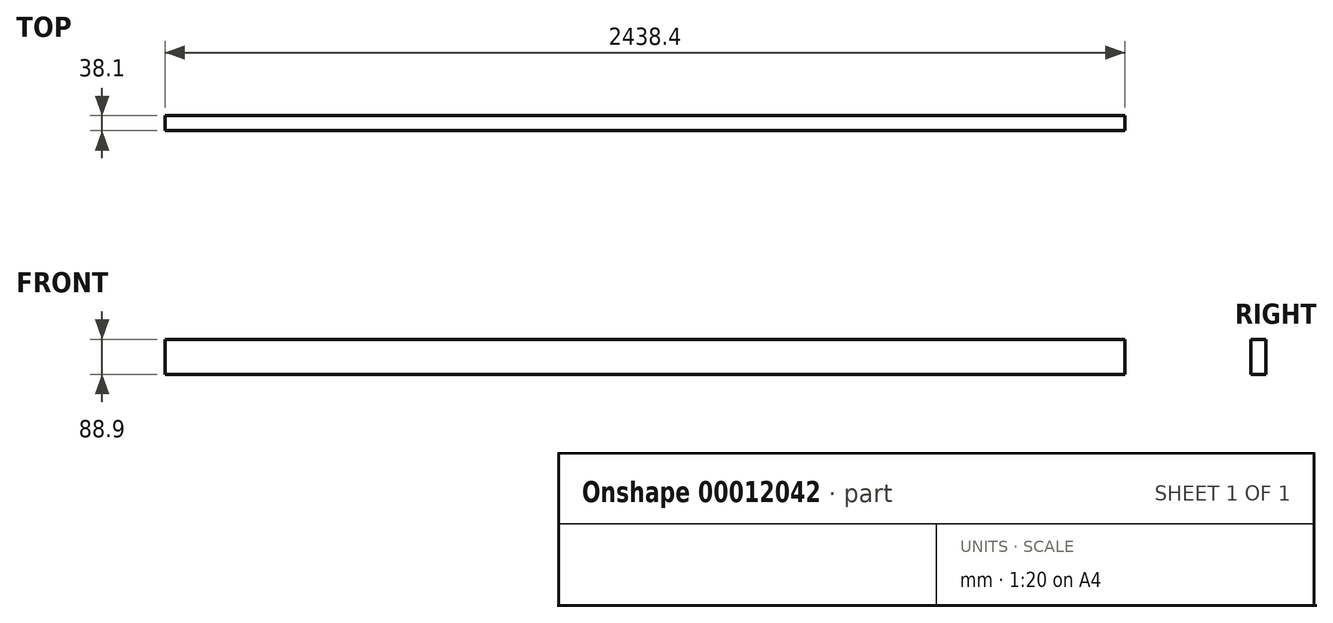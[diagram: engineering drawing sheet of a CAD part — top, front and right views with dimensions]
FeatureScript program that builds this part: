
annotation { "Feature Type Name" : "Feature", "Feature Type Description" : "" }
export const myFeature = defineFeature(function(context is Context, id is Id, definition is map)
    precondition{}
    {
        {
            var Q0;
            Q0=qCreatedBy(makeId("Right.planeOp"),FACE);
            var sketch = newSketch(context, id + "F1", { "sketchPlane" : qUnion([Q0])});
            skLineSegment(sketch, "E0.rect.bottom", {"start": v(19.05, 44.45) * mm, "end": v(-19.05, 44.45) * mm});
            skLineSegment(sketch, "E0.rect.top", {"start": v(19.05, -44.45) * mm, "end": v(-19.05, -44.45) * mm});
            skLineSegment(sketch, "E0.rect.left", {"start": v(19.05, 44.45) * mm, "end": v(19.05, -44.45) * mm});
            skLineSegment(sketch, "E0.rect.right", {"start": v(-19.05, 44.45) * mm, "end": v(-19.05, -44.45) * mm});
            skPoint(sketch, "E0.rect.middle", {"position": v(0, 0) * mm});
            skSolve(sketch);
        }
        {
            var Q0;
            Q0=makeQuery(id+"F1.imprint","IMPRINT",FACE,{"disambiguationData":[TD([[makeQuery(id+"F1.imprint","IMPRINT",EDGE,{"derivedFrom":sQuery(id+"F1.wireOp",EDGE,"E0.rect.bottom")}),1.0]])]});
            extrude(context, id + "F0", {"entities" : qUnion([Q0]), "depth" : 2438.4 * mm});
        }
    });
